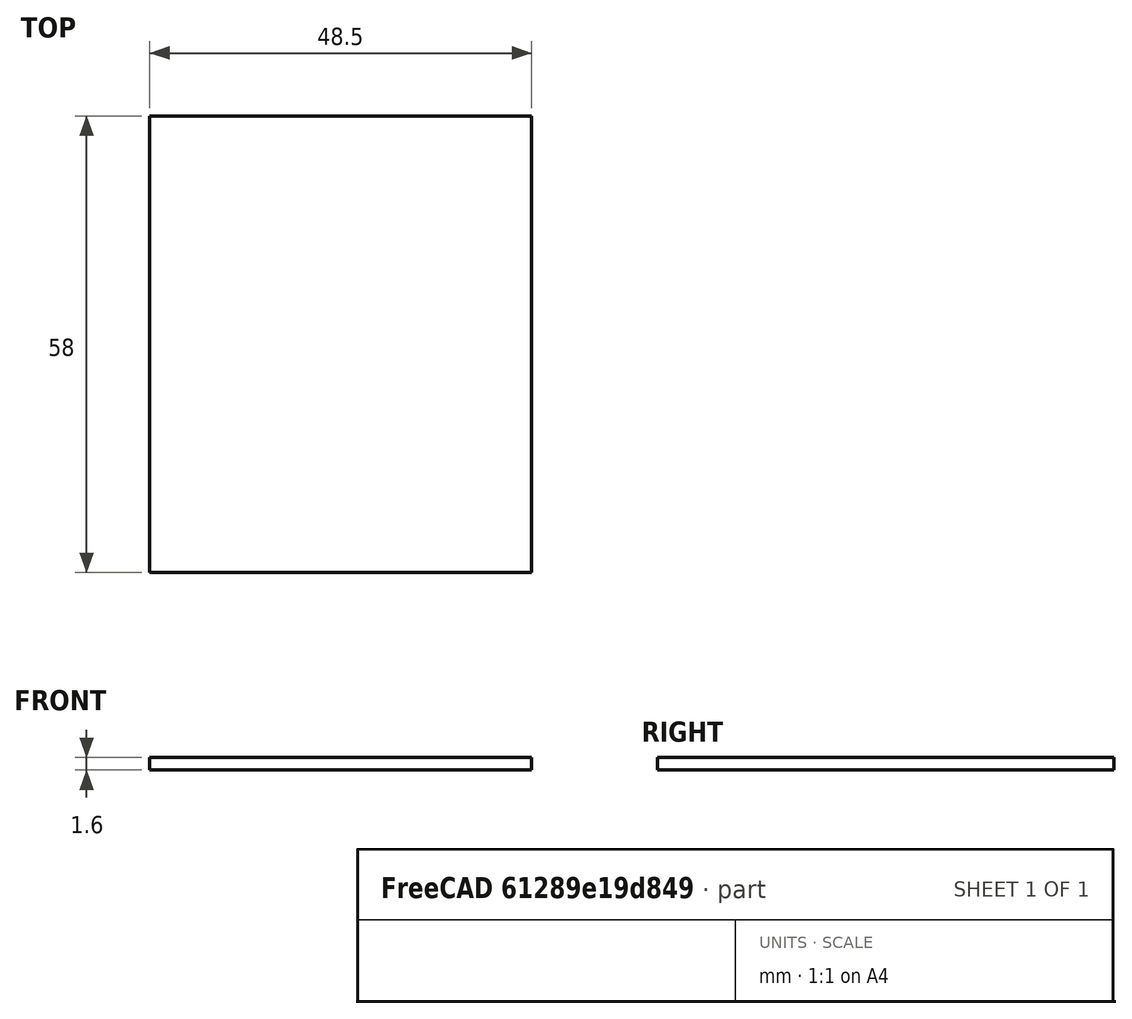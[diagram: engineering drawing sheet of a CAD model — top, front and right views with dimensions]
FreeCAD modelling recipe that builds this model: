
FCSTD DOCUMENT  (FreeCAD 0.19R24276 (Git))
Label: pir-baffel-bottomFront
License: All rights reserved
LicenseURL: http://en.wikipedia.org/wiki/All_rights_reserved
objects: Sketcher::SketchObject×1, PartDesign::Pad×1, PartDesign::CoordinateSystem×1, PartDesign::Body×1
note: 5 computed .brp shape members not serialized (recipe doc carries the construction recipe); baked Part::Feature solids carry a one-line shape summary decoded from their .brp

FEATURE [Sketcher::SketchObject] Sketch
  FullyConstrained = true
  MapMode = 5
  Support = -> [XY_Plane]
  sketch-geometry (4):
    g0: LineSegment StartX=-24.25 StartY=29 StartZ=0 EndX=24.25 EndY=29 EndZ=0
    g1: LineSegment StartX=24.25 StartY=29 StartZ=0 EndX=24.25 EndY=-29 EndZ=0
    g2: LineSegment StartX=24.25 StartY=-29 StartZ=0 EndX=-24.25 EndY=-29 EndZ=0
    g3: LineSegment StartX=-24.25 StartY=-29 StartZ=0 EndX=-24.25 EndY=29 EndZ=0
  constraints (10):
    c: Coincident(g0,g1)
    c: Coincident(g1,g2)
    c: Coincident(g2,g3)
    c: Coincident(g3,g0)
    c: Horizontal(g2)
    c: Vertical(g3)
    c: DistanceY(g3,g3) = 58
    c: DistanceX(g0,g0) = 48.5
    c: Symmetric(g0,g0,g-2)
    c: Symmetric(g0,g1,g-1)
FEATURE [PartDesign::Pad] Pad  label="BottomFront"
  Direction = (1,1,1)
  Length = 1.6
  Length2 = 100
  Profile = -> Sketch
  Type = 0
FEATURE [PartDesign::CoordinateSystem] LCS_bottomFront
  AttacherType = Attacher::AttachEngine3D
  MapMode = 45
  Placement = pos=(1e-16,29,0.8) rot=(0.57735,0.57735,0.57735;4.18879rad)
  Support = -> [Pad]
FEATURE [PartDesign::Body] Body
  Group = -> [Sketch,Pad,LCS_bottomFront]
  Origin = -> Origin
  Tip = -> Pad
